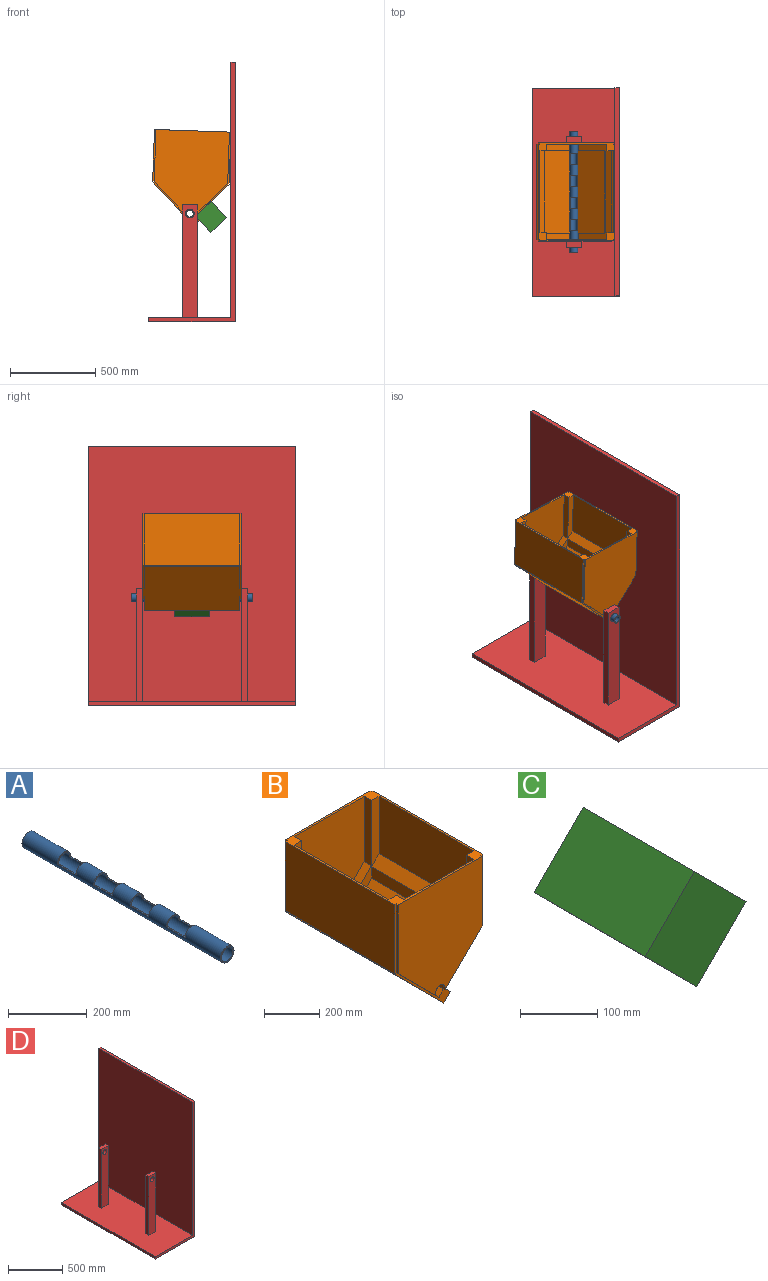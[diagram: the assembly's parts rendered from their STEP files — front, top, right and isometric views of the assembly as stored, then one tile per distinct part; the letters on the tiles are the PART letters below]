
ASSEMBLY  parts=4 mates=3
PART A: 20 faces, bbox 48.3x711.2x48.3 mm
  f0: cylinder r=20.45mm len=711.2mm, axis (0,1,0), area 74237.7mm2, adj f2,f3,f4,f5,f6,f7,f8,f9
  f1: cylinder r=24.13mm len=711.2mm, axis (0,1,0), area 87609.7mm2, adj f2,f3,f4,f5,f6,f7,f8,f9
  f2: plane 48.26x48.26mm, normal (0,-1,0), area 515.8mm2, adj f0,f1
  f3: plane 48.26x48.26mm, normal (0,1,0), area 515.8mm2, adj f0,f1
  f4: plane 48.26x24.13mm, normal (0,1,0), area 257.9mm2, adj f0,f1,f5,f6
  f5: plane 66.68x3.68mm, normal (0,0,1), area 245.6mm2, adj f0,f1,f4,f7
  f6: plane 66.68x3.68mm, normal (0,0,1), area 245.6mm2, adj f0,f1,f4,f7
  f7: plane 48.26x24.13mm, normal (0,-1,0), area 257.9mm2, adj f0,f1,f5,f6
  f8: plane 48.26x24.13mm, normal (0,1,0), area 257.9mm2, adj f0,f1,f9,f10
  f9: plane 66.68x3.68mm, normal (0,0,1), area 245.6mm2, adj f0,f1,f8,f11
  f10: plane 66.68x3.68mm, normal (0,0,1), area 245.6mm2, adj f0,f1,f8,f11
  f11: plane 48.26x24.13mm, normal (0,-1,0), area 257.9mm2, adj f0,f1,f9,f10
  f12: plane 48.26x24.13mm, normal (0,1,0), area 257.9mm2, adj f0,f1,f13,f14
  f13: plane 66.68x3.68mm, normal (0,0,1), area 245.6mm2, adj f0,f1,f12,f15
  f14: plane 66.68x3.68mm, normal (0,0,1), area 245.6mm2, adj f0,f1,f12,f15
  f15: plane 48.26x24.13mm, normal (0,-1,0), area 257.9mm2, adj f0,f1,f13,f14
  f16: plane 48.26x24.13mm, normal (0,1,0), area 257.9mm2, adj f0,f1,f17,f18
  f17: plane 66.68x3.68mm, normal (0,0,1), area 245.6mm2, adj f0,f1,f16,f19
  f18: plane 66.68x3.68mm, normal (0,0,1), area 245.6mm2, adj f0,f1,f16,f19
  f19: plane 48.26x24.13mm, normal (0,-1,0), area 257.9mm2, adj f0,f1,f17,f18
PART B: 57 faces, bbox 449.3x576.3x560 mm
  f0: plane 444.16x255.2mm, normal (0,1,0), area 7191.9mm2, adj f10,f13,f14,f15,f19,f20,f21,f22
  f1: plane 304.8x8.74mm, normal (0,1,0), area 2663.2mm2, adj f16,f25,f26,f54
  f2: plane 304.8x8.74mm, normal (0,1,0), area 2663.2mm2, adj f16,f17,f18,f53
  f3: plane 482.6x50.8mm, normal (1,0,0), area 24516.1mm2, adj f4,f10,f34,f49
  f4: plane 482.6x38.1mm, normal (0.71,0,0.71), area 26003.2mm2, adj f3,f11,f34,f49
  f5: plane 482.6x38.1mm, normal (-0.71,0,0.71), area 26003.2mm2, adj f6,f12,f30,f45
  f6: plane 482.6x50.8mm, normal (-1,0,0), area 24516.1mm2, adj f5,f13,f30,f45
  f7: plane 444.16x255.2mm, normal (0,-1,0), area 7191.9mm2, adj f10,f13,f14,f15,f19,f20,f21,f22
  f8: plane 304.8x8.74mm, normal (0,-1,0), area 2663.2mm2, adj f16,f25,f26,f38
  f9: plane 304.8x8.74mm, normal (0,-1,0), area 2663.2mm2, adj f16,f17,f18,f39
  f10: plane 558.8x183.98mm, normal (0.71,0,0.71), area 128831.3mm2, adj f0,f3,f7,f15,f31,f34,f48,f49
  f11: plane 482.6x254mm, normal (1,0,0), area 122580.4mm2, adj f4,f16,f34,f49
  f12: plane 482.6x254mm, normal (-1,0,0), area 122580.4mm2, adj f5,f16,f30,f45
  f13: plane 558.8x177.43mm, normal (-0.71,0,0.71), area 123653.3mm2, adj f0,f6,f7,f14,f29,f30,f42,f45
  f14: plane 558.8x6.18mm, normal (-0.71,0,-0.71), area 4882.6mm2, adj f0,f7,f13,f15
  f15: plane 558.8x0.37mm, normal (-0.71,0,0.71), area 295.4mm2, adj f0,f7,f10,f14
  f16: plane 576.28x449.28mm, normal (0,0,1), area 23117.4mm2, adj f1,f2,f8,f9,f11,f12,f17,f26
  f17: plane 558.8x304.8mm, normal (-1,0,0), area 170322.2mm2, adj f2,f9,f16,f18
  f18: plane 558.8x8.74mm, normal (0,0,-1), area 4882.6mm2, adj f2,f9,f17,f19
  f19: plane 558.8x6.18mm, normal (-0.71,0,0.71), area 4882.6mm2, adj f0,f7,f18,f20
  f20: plane 558.8x249.02mm, normal (-0.71,0,-0.71), area 196790.5mm2, adj f0,f7,f19,f21
  f21: plane 558.8x33.12mm, normal (0.71,0,-0.71), area 26172.9mm2, adj f0,f7,f20,f22
  f22: plane 558.8x26.94mm, normal (0.71,0,0.71), area 21290.3mm2, adj f0,f7,f21,f23
  f23: plane 558.8x188.96mm, normal (0.71,0,-0.71), area 149327.4mm2, adj f0,f7,f22,f24
  f24: plane 558.8x6.18mm, normal (0.71,0,0.71), area 4882.6mm2, adj f0,f7,f23,f25
  f25: plane 558.8x8.74mm, normal (0,0,-1), area 4882.6mm2, adj f1,f8,f24,f26
  f26: plane 558.8x304.8mm, normal (1,0,0), area 170322.2mm2, adj f1,f8,f16,f25
  f27: plane 289.02x38.1mm, normal (-1,0,0), area 11011.6mm2, adj f16,f28,f30,f35
  f28: plane 153.67x153.67mm, normal (-0.71,0,0.71), area 8280mm2, adj f27,f29,f30,f35
  f29: plane 53.88x46.84mm, normal (-1,0,0), area 2140.2mm2, adj f13,f28,f30,f35,f36,f37,f41
  f30: plane 496.57x191.77mm, normal (0,1,0), area 18683.2mm2, adj f5,f6,f12,f13,f16,f27,f28,f29
  f31: plane 53.88x46.84mm, normal (1,0,0), area 2140.2mm2, adj f10,f32,f34,f35,f36,f40,f41
  f32: plane 153.67x153.67mm, normal (0.71,0,0.71), area 8280mm2, adj f31,f33,f34,f35
  f33: plane 289.02x38.1mm, normal (1,0,0), area 11011.6mm2, adj f16,f32,f34,f35
  f34: plane 496.57x191.77mm, normal (0,1,0), area 18683.2mm2, adj f3,f4,f10,f11,f16,f31,f32,f33
  f35: plane 486.58x355.6mm, normal (0,1,0), area 135008.9mm2, adj f16,f27,f28,f29,f31,f32,f33,f36
  f36: cylinder r=24.13mm len=48.26mm, axis (0,1,0), area 662.4mm2, adj f29,f31,f35,f41
  f37: plane 191.77x191.77mm, normal (0.71,0,-0.71), area 2369.7mm2, adj f7,f29,f38,f41
  f38: plane 304.8x8.74mm, normal (1,0,0), area 2663.2mm2, adj f8,f16,f37,f41
  f39: plane 304.8x8.74mm, normal (-1,0,0), area 2663.2mm2, adj f9,f16,f40,f41
  f40: plane 191.77x191.77mm, normal (-0.71,0,-0.71), area 2369.7mm2, adj f7,f31,f39,f41
  f41: plane 496.57x431.8mm, normal (0,-1,0), area 176246.2mm2, adj f16,f29,f31,f36,f37,f38,f39,f40
  f42: plane 53.88x46.84mm, normal (-1,0,0), area 2140.2mm2, adj f13,f43,f45,f50,f51,f55,f56
  f43: plane 153.67x153.67mm, normal (-0.71,0,0.71), area 8280mm2, adj f42,f44,f45,f50
  f44: plane 289.02x38.1mm, normal (-1,0,0), area 11011.6mm2, adj f16,f43,f45,f50
  f45: plane 496.57x191.77mm, normal (0,-1,0), area 18683.2mm2, adj f5,f6,f12,f13,f16,f42,f43,f44
  f46: plane 289.02x38.1mm, normal (1,0,0), area 11011.6mm2, adj f16,f47,f49,f50
  f47: plane 153.67x153.67mm, normal (0.71,0,0.71), area 8280mm2, adj f46,f48,f49,f50
  f48: plane 53.88x46.84mm, normal (1,0,0), area 2140.2mm2, adj f10,f47,f49,f50,f51,f52,f56
  f49: plane 496.57x191.77mm, normal (0,-1,0), area 18683.2mm2, adj f3,f4,f10,f11,f16,f46,f47,f48
  f50: plane 486.58x355.6mm, normal (0,-1,0), area 135008.9mm2, adj f16,f42,f43,f44,f46,f47,f48,f51
  f51: cylinder r=24.13mm len=48.26mm, axis (0,-1,0), area 662.4mm2, adj f42,f48,f50,f56
  f52: plane 191.77x191.77mm, normal (-0.71,0,-0.71), area 2369.7mm2, adj f0,f48,f53,f56
  f53: plane 304.8x8.74mm, normal (-1,0,0), area 2663.2mm2, adj f2,f16,f52,f56
  f54: plane 304.8x8.74mm, normal (1,0,0), area 2663.2mm2, adj f1,f16,f55,f56
  f55: plane 191.77x191.77mm, normal (0.71,0,-0.71), area 2369.7mm2, adj f0,f42,f54,f56
  f56: plane 496.57x431.8mm, normal (0,1,0), area 176246.2mm2, adj f16,f42,f48,f51,f52,f53,f54,f55
PART C: 6 faces, bbox 184.1x203.2x184.1 mm
  f0: plane 203.2x89.8mm, normal (-0.71,0,0.71), area 25806.4mm2, adj f1,f3,f4,f5
  f1: plane 203.2x94.29mm, normal (-0.71,0,-0.71), area 27096.7mm2, adj f0,f2,f4,f5
  f2: plane 203.2x89.8mm, normal (0.71,0,-0.71), area 25806.4mm2, adj f1,f3,f4,f5
  f3: plane 203.2x94.29mm, normal (0.71,0,0.71), area 27096.7mm2, adj f0,f2,f4,f5
  f4: plane 184.1x184.1mm, normal (0,-1,0), area 16935.4mm2, adj f0,f1,f2,f3
  f5: plane 184.1x184.1mm, normal (0,1,0), area 16935.4mm2, adj f0,f1,f2,f3
PART D: 20 faces, bbox 508x1219.2x1524 mm
  f0: plane 660.4x38.1mm, normal (1,0,0), area 25161.2mm2, adj f1,f4,f5,f12
  f1: plane 88.9x38.1mm, normal (0,0,1), area 3387.1mm2, adj f0,f2,f4,f5
  f2: plane 660.4x38.1mm, normal (-1,0,0), area 25161.2mm2, adj f1,f4,f5,f12
  f3: cylinder r=25.4mm len=50.8mm, axis (0,1,0), area 6080.5mm2, adj f4,f5
  f4: plane 660.4x88.9mm, normal (0,-1,0), area 56682.7mm2, adj f0,f1,f2,f3,f12
  f5: plane 660.4x88.9mm, normal (0,1,0), area 56682.7mm2, adj f0,f1,f2,f3,f12
  f6: plane 660.4x38.1mm, normal (1,0,0), area 25161.2mm2, adj f7,f10,f11,f12
  f7: plane 88.9x38.1mm, normal (0,0,1), area 3387.1mm2, adj f6,f8,f10,f11
  f8: plane 660.4x38.1mm, normal (-1,0,0), area 25161.2mm2, adj f7,f10,f11,f12
  f9: cylinder r=25.4mm len=50.8mm, axis (0,-1,0), area 6080.5mm2, adj f10,f11
  f10: plane 660.4x88.9mm, normal (0,1,0), area 56682.7mm2, adj f6,f7,f8,f9,f12
  f11: plane 660.4x88.9mm, normal (0,-1,0), area 56682.7mm2, adj f6,f7,f8,f9,f12
  f12: plane 1219.2x482.6mm, normal (0,0,1), area 581611.7mm2, adj f0,f2,f4,f5,f6,f8,f10,f11
  f13: plane 1219.2x25.4mm, normal (-1,0,0), area 30967.7mm2, adj f12,f14,f18,f19
  f14: plane 1219.2x508mm, normal (0,0,-1), area 619353.6mm2, adj f13,f15,f18,f19
  f15: plane 1524x1219.2mm, normal (1,0,0), area 1858060.8mm2, adj f14,f16,f18,f19
  f16: plane 1219.2x25.4mm, normal (0,0,1), area 30967.7mm2, adj f15,f17,f18,f19
  f17: plane 1498.6x1219.2mm, normal (-1,0,0), area 1827093.1mm2, adj f12,f16,f18,f19
  f18: plane 1524x508mm, normal (0,-1,0), area 50967.6mm2, adj f12,f13,f14,f15,f16,f17
  f19: plane 1524x508mm, normal (0,1,0), area 50967.6mm2, adj f12,f13,f14,f15,f16,f17
PLACE A rot(axis=(0,1,0),2deg) t=(0,0,0)mm
PLACE B rot(axis=(0,1,0),2deg) t=(0,0,0)mm
PLACE C rot(axis=(0.69,0,-0.72),180deg) t=(113.28,0,105.71)mm
PLACE D at identity fixed
MATE revolute B.f36 <-> D.f3  axis (0,-1,0) through (0,0,0)mm
MATE fastened C.f0 <-> B.f23  axis (-0.68,0,0.73) through (79.06,0,28.83)mm
MATE fastened A.f0 <-> B.f36  axis (0,-1,0) through (0,0,0)mm
